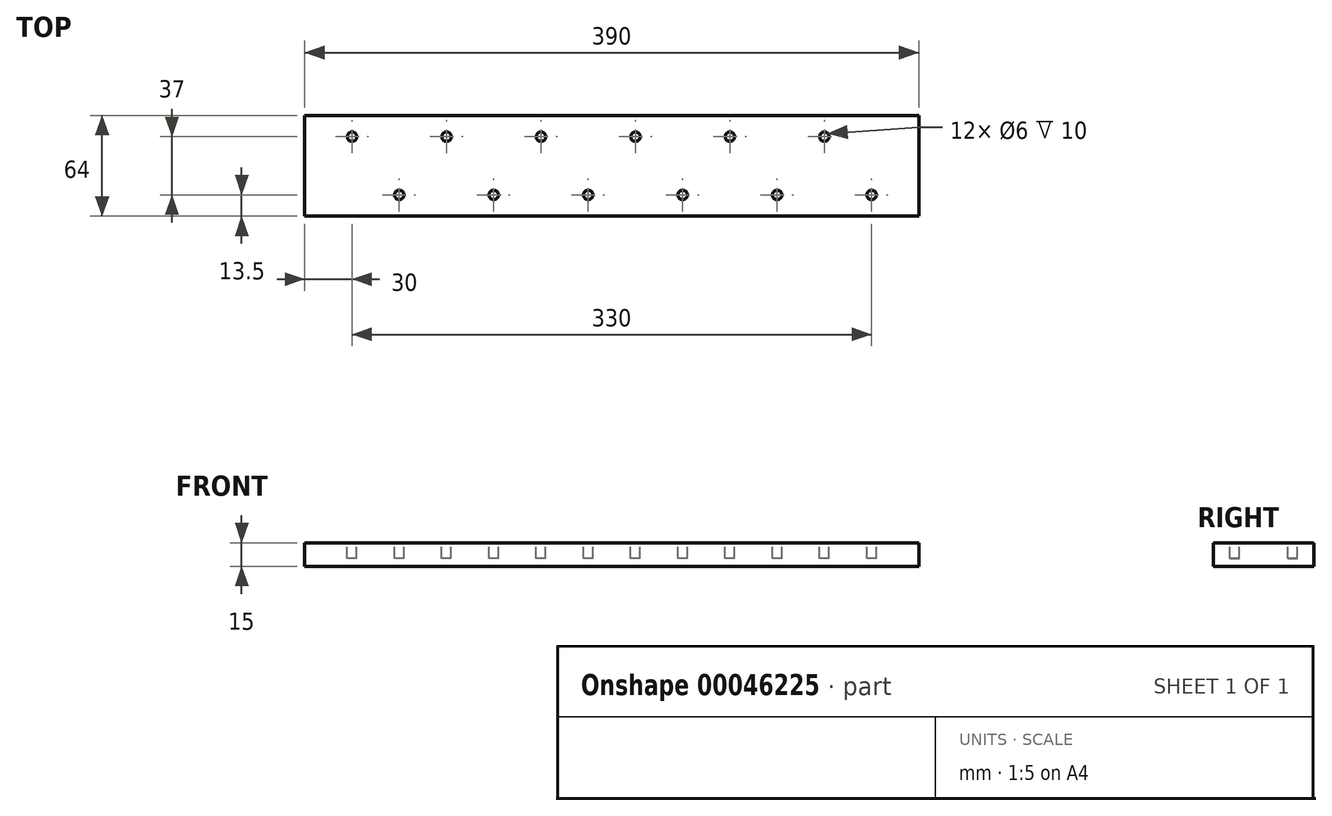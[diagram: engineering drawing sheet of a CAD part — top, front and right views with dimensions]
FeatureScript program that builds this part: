
annotation { "Feature Type Name" : "Feature", "Feature Type Description" : "" }
export const myFeature = defineFeature(function(context is Context, id is Id, definition is map)
    precondition{}
    {
        {
            var Q0;
            Q0=qCreatedBy(makeId("Top.planeOp"),FACE);
            var sketch = newSketch(context, id + "F0", { "sketchPlane" : qUnion([Q0])});
            skLineSegment(sketch, "E0.bottom", {"start": v(0, 0) * mm, "end": v(390, 0) * mm});
            skLineSegment(sketch, "E0.top", {"start": v(0, 64) * mm, "end": v(390, 64) * mm});
            skLineSegment(sketch, "E0.left", {"start": v(0, 0) * mm, "end": v(0, 64) * mm});
            skLineSegment(sketch, "E0.right", {"start": v(390, 0) * mm, "end": v(390, 64) * mm});
            skSolve(sketch);
        }
        {
            var Q0;
            Q0=makeQuery(id+"F0.imprint","IMPRINT",FACE,{"disambiguationData":[TD([[makeQuery(id+"F0.imprint","IMPRINT",EDGE,{"derivedFrom":sQuery(id+"F0.wireOp",EDGE,"E0.bottom")}),1.0]])]});
            extrude(context, id + "F1", {"entities" : qUnion([Q0]), "depth" : 15 * mm});
        }
        {
            var Q0;
            Q0=makeQuery(id+"F1.opExtrude","CAP_FACE",FACE,{"disambiguationData":[OSD([sQuery(id+"F0.wireOp",EDGE,"E0.bottom"),sQuery(id+"F0.wireOp",EDGE,"E0.top"),sQuery(id+"F0.wireOp",EDGE,"E0.left"),sQuery(id+"F0.wireOp",EDGE,"E0.right")])],"isStart":false});
            var sketch = newSketch(context, id + "F2", { "sketchPlane" : qUnion([Q0])});
            skLineSegment(sketch, "E1.0.0", {"start": v(0, 64) * mm, "end": v(0, 0) * mm});
            skLineSegment(sketch, "E1.0.1", {"start": v(0, 0) * mm, "end": v(390, 0) * mm});
            skLineSegment(sketch, "E1.0.2", {"start": v(390, 0) * mm, "end": v(390, 64) * mm});
            skLineSegment(sketch, "E1.0.3", {"start": v(390, 64) * mm, "end": v(0, 64) * mm});
            skCircle(sketch, "E2", {"center": v(30, 50.5) * mm, "radius": 3 * mm});
            skCircle(sketch, "E3", {"center": v(60, 13.5) * mm, "radius": 3 * mm});
            skCircle(sketch, "E4", {"center": v(90, 50.5) * mm, "radius": 3 * mm});
            skCircle(sketch, "E5", {"center": v(150, 50.5) * mm, "radius": 3 * mm});
            skCircle(sketch, "E6", {"center": v(210, 50.5) * mm, "radius": 3 * mm});
            skCircle(sketch, "E7", {"center": v(270, 50.5) * mm, "radius": 3 * mm});
            skCircle(sketch, "E8", {"center": v(330, 50.5) * mm, "radius": 3 * mm});
            skCircle(sketch, "E9", {"center": v(120, 13.5) * mm, "radius": 3 * mm});
            skCircle(sketch, "E10", {"center": v(180, 13.5) * mm, "radius": 3 * mm});
            skCircle(sketch, "E11", {"center": v(240, 13.5) * mm, "radius": 3 * mm});
            skCircle(sketch, "E12", {"center": v(300, 13.5) * mm, "radius": 3 * mm});
            skCircle(sketch, "E13", {"center": v(360, 13.5) * mm, "radius": 3 * mm});
            skSolve(sketch);
        }
        {
            var Q0;
            Q0=makeQuery(id+"F2.imprint","IMPRINT",FACE,{"disambiguationData":[TD([[makeQuery(id+"F2.imprint","IMPRINT",EDGE,{"derivedFrom":sQuery(id+"F2.wireOp",EDGE,"E2")}),1.0]])]});
            var Q1;
            Q1=makeQuery(id+"F2.imprint","IMPRINT",FACE,{"disambiguationData":[TD([[makeQuery(id+"F2.imprint","IMPRINT",EDGE,{"derivedFrom":sQuery(id+"F2.wireOp",EDGE,"E3")}),1.0]])]});
            var Q2;
            Q2=makeQuery(id+"F2.imprint","IMPRINT",FACE,{"disambiguationData":[TD([[makeQuery(id+"F2.imprint","IMPRINT",EDGE,{"derivedFrom":sQuery(id+"F2.wireOp",EDGE,"E4")}),1.0]])]});
            var Q3;
            Q3=makeQuery(id+"F2.imprint","IMPRINT",FACE,{"disambiguationData":[TD([[makeQuery(id+"F2.imprint","IMPRINT",EDGE,{"derivedFrom":sQuery(id+"F2.wireOp",EDGE,"E9")}),1.0]])]});
            var Q4;
            Q4=makeQuery(id+"F2.imprint","IMPRINT",FACE,{"disambiguationData":[TD([[makeQuery(id+"F2.imprint","IMPRINT",EDGE,{"derivedFrom":sQuery(id+"F2.wireOp",EDGE,"E5")}),1.0]])]});
            var Q5;
            Q5=makeQuery(id+"F2.imprint","IMPRINT",FACE,{"disambiguationData":[TD([[makeQuery(id+"F2.imprint","IMPRINT",EDGE,{"derivedFrom":sQuery(id+"F2.wireOp",EDGE,"E10")}),1.0]])]});
            var Q6;
            Q6=makeQuery(id+"F2.imprint","IMPRINT",FACE,{"disambiguationData":[TD([[makeQuery(id+"F2.imprint","IMPRINT",EDGE,{"derivedFrom":sQuery(id+"F2.wireOp",EDGE,"E6")}),1.0]])]});
            var Q7;
            Q7=makeQuery(id+"F2.imprint","IMPRINT",FACE,{"disambiguationData":[TD([[makeQuery(id+"F2.imprint","IMPRINT",EDGE,{"derivedFrom":sQuery(id+"F2.wireOp",EDGE,"E11")}),1.0]])]});
            var Q8;
            Q8=makeQuery(id+"F2.imprint","IMPRINT",FACE,{"disambiguationData":[TD([[makeQuery(id+"F2.imprint","IMPRINT",EDGE,{"derivedFrom":sQuery(id+"F2.wireOp",EDGE,"E7")}),1.0]])]});
            var Q9;
            Q9=makeQuery(id+"F2.imprint","IMPRINT",FACE,{"disambiguationData":[TD([[makeQuery(id+"F2.imprint","IMPRINT",EDGE,{"derivedFrom":sQuery(id+"F2.wireOp",EDGE,"E12")}),1.0]])]});
            var Q10;
            Q10=makeQuery(id+"F2.imprint","IMPRINT",FACE,{"disambiguationData":[TD([[makeQuery(id+"F2.imprint","IMPRINT",EDGE,{"derivedFrom":sQuery(id+"F2.wireOp",EDGE,"E8")}),1.0]])]});
            var Q11;
            Q11=makeQuery(id+"F2.imprint","IMPRINT",FACE,{"disambiguationData":[TD([[makeQuery(id+"F2.imprint","IMPRINT",EDGE,{"derivedFrom":sQuery(id+"F2.wireOp",EDGE,"E13")}),1.0]])]});
            extrude(context, id + "F3", {"entities" : qUnion([Q0, Q1, Q2, Q3, Q4, Q5, Q6, Q7, Q8, Q9, Q10, Q11]), "operationType" : NewBodyOperationType.REMOVE, "oppositeDirection" : true, "depth" : 10 * mm});
        }
    });
